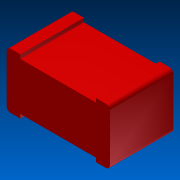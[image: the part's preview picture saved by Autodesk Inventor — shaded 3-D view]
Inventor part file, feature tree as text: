
AUTODESK INVENTOR PART (.ipt)
format: ipt  version: 2011 SP1 (Build 150282100, 282)  size: 104,448 bytes
history: native  units: mm
features: extrude x2, sketch x2, fillet x1, reference x1
ambient origin geometry x8: Origin, YZ Plane, XZ Plane, XY Plane, X Axis, Y Axis, Z Axis, Center Point
bodies: Solid1 (feature_tree)
feature tree (6):
  extrude  "Extrusion1"  Depth=13.0mm
  extrude  "Extrusion2"  Depth=0.5mm
  fillet  "Fillet1"  Radius=0.5mm
  sketch  "Sketch1"  dims[d0=8.0mm d1=13.0mm]
  sketch  "Sketch2"  dims[d2=7.0mm d3=0.0mm d4=0.5mm d5=0.5mm d6=9.55mm d7=9.55mm d8=7.0mm d9=0.0mm d10=0.5mm]
  reference  "Reference2"
